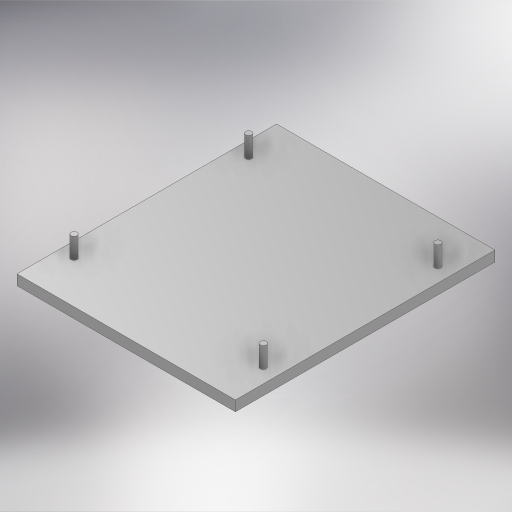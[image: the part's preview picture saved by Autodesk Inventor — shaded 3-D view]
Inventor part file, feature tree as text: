
AUTODESK INVENTOR PART (.ipt)
format: ipt  version: 2024 (Build 280153000, 153)  size: 342,528 bytes
history: native  units: mm
features: other x11, extrude x3, sketch x3
ambient origin geometry x8: Origin, YZ Plane, XZ Plane, XY Plane, X Axis, Y Axis, Z Axis, Center Point
bodies: Body1 (feature_tree)
feature tree (17):
  other  "Sólido1"
  extrude  "Extrusión1"  Depth=126.0mm
  extrude  "Extrusión2"  Depth=53.0mm
  extrude  "Extrusión3"  Depth=3.0mm
  sketch  "Boceto1"  dims[d1=106.0mm d2=126.0mm]
  sketch  "Boceto2"  dims[d3=53.0mm d4=63.0mm]
  sketch  "Boceto3"  dims[d5=5.0mm d6=0.0mm d7=3.0mm d8=20.616mm d9=7.071mm d10=10.0mm d11=0.0mm d12=52.5mm d13=126.0mm d14=106.0mm d15=52.5mm d16=35.0mm d17=35.0mm d18=35.0mm d19=35.0mm d20=35.0mm d21=2.0mm d22=0.0mm]
  other  "Finish1"
  other  "Finish2"
  other  "Finish3"
  other  "Finish4"
  other  "Finish5"
  other  "Finish6"
  other  "Finish7"
  other  "Finish8"
  other  "Finish9"
  other  "Finish10"
